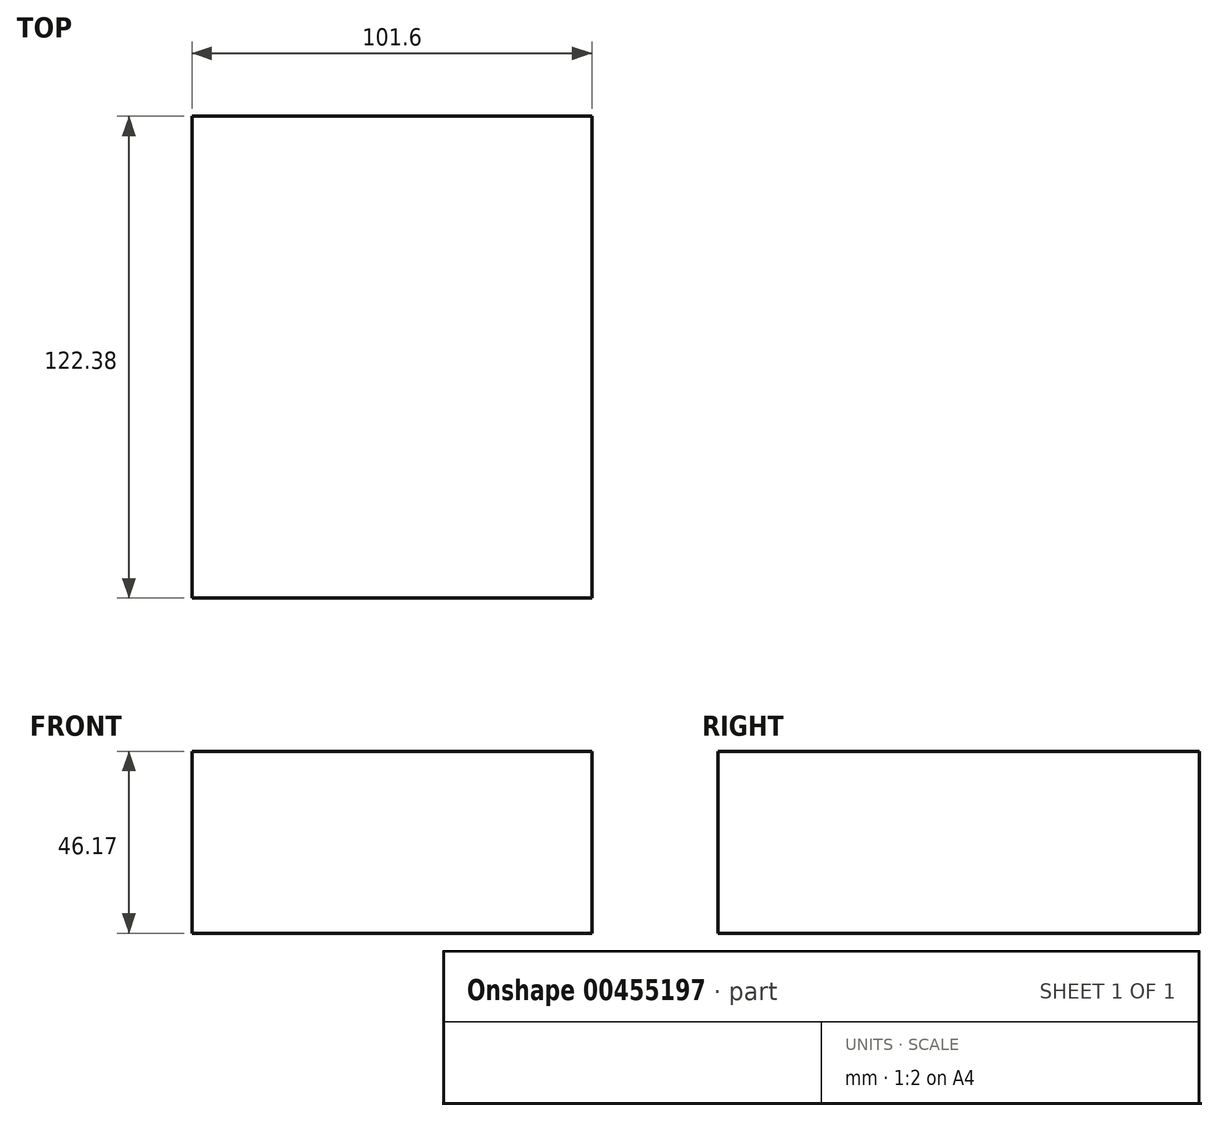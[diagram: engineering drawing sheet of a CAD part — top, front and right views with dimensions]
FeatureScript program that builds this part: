
annotation { "Feature Type Name" : "Feature", "Feature Type Description" : "" }
export const myFeature = defineFeature(function(context is Context, id is Id, definition is map)
    precondition{}
    {
        {
            var Q0;
            Q0=qCreatedBy(makeId("Right.planeOp"),FACE);
            var sketch = newSketch(context, id + "F0", { "sketchPlane" : qUnion([Q0])});
            skLineSegment(sketch, "E0.bottom", {"start": v(0, 15.42) * mm, "end": v(122.38, 15.42) * mm});
            skLineSegment(sketch, "E0.top", {"start": v(0, -30.75) * mm, "end": v(122.38, -30.75) * mm});
            skLineSegment(sketch, "E0.left", {"start": v(0, 15.42) * mm, "end": v(0, -30.75) * mm});
            skLineSegment(sketch, "E0.right", {"start": v(122.38, 15.42) * mm, "end": v(122.38, -30.75) * mm});
            skSolve(sketch);
        }
        {
            var Q0;
            Q0=sQuery(id+"F0.wireOp",EDGE,"E0.right");
            var Q1;
            Q1=sQuery(id+"F0.wireOp",EDGE,"E0.left");
            var Q2;
            Q2=sQuery(id+"F0.wireOp",EDGE,"E0.bottom");
            var Q3;
            Q3=sQuery(id+"F0.wireOp",EDGE,"E0.top");
            extrude(context, id + "F1", {"bodyType" : ToolBodyType.SURFACE, "surfaceEntities" : qUnion([Q0, Q1, Q2, Q3]), "depth" : 101.6 * mm});
        }
    });
